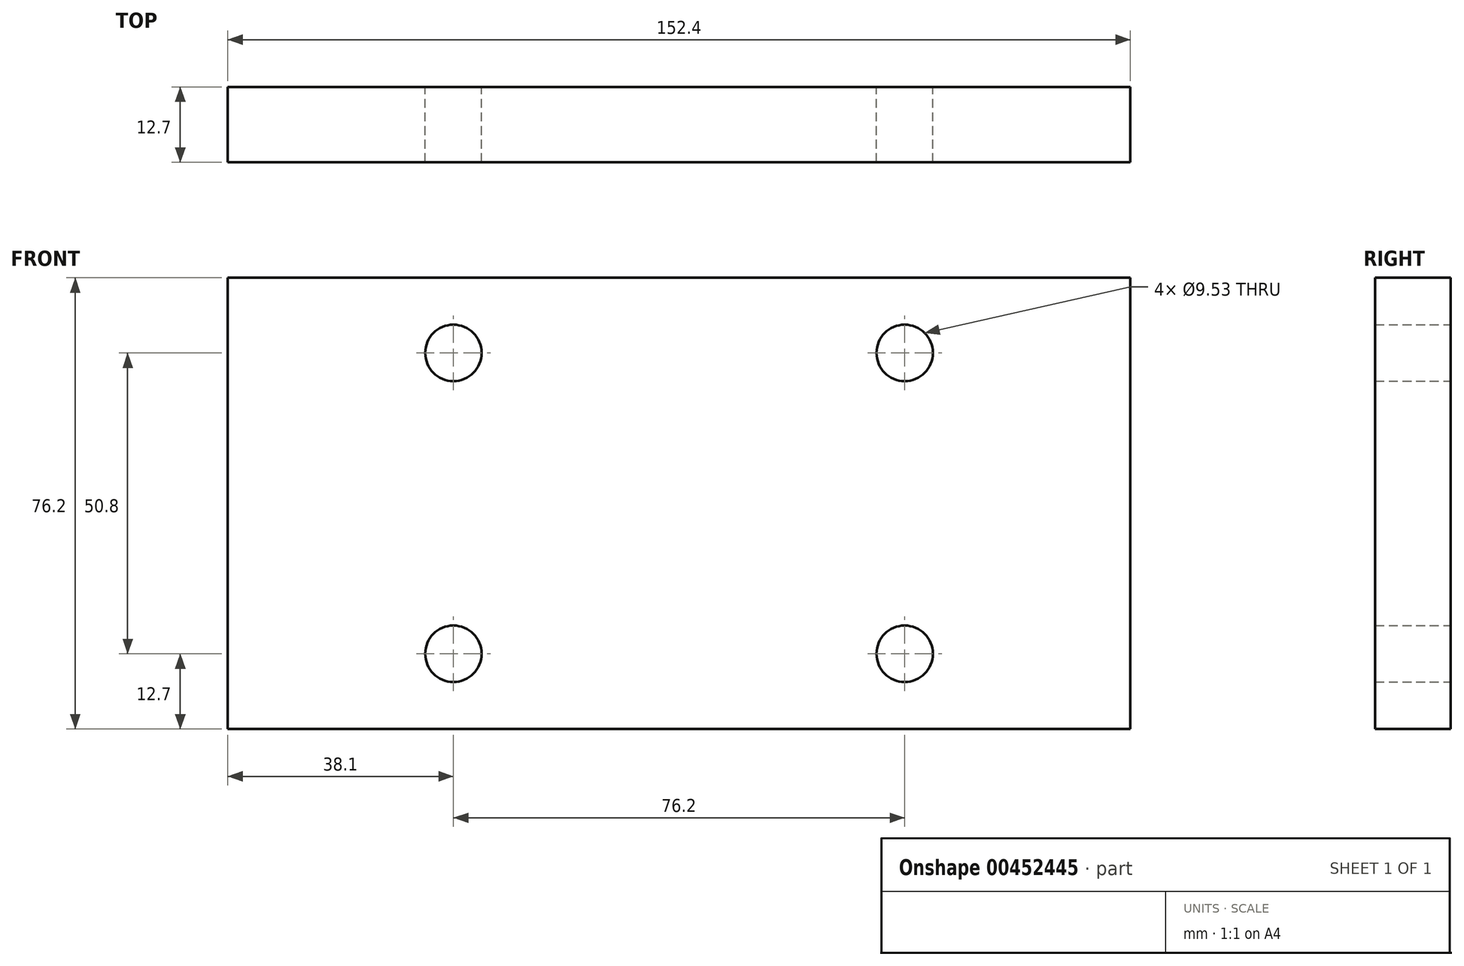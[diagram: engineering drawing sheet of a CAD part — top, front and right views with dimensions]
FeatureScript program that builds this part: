
annotation { "Feature Type Name" : "Feature", "Feature Type Description" : "" }
export const myFeature = defineFeature(function(context is Context, id is Id, definition is map)
    precondition{}
    {
        {
            var Q0;
            Q0=qCreatedBy(makeId("Front.planeOp"),FACE);
            var sketch = newSketch(context, id + "F0", { "sketchPlane" : qUnion([Q0])});
            skLineSegment(sketch, "E0.bottom", {"start": v(0, 0) * mm, "end": v(152.4, 0) * mm});
            skLineSegment(sketch, "E0.top", {"start": v(0, 76.2) * mm, "end": v(152.4, 76.2) * mm});
            skLineSegment(sketch, "E0.left", {"start": v(0, 0) * mm, "end": v(0, 76.2) * mm});
            skLineSegment(sketch, "E0.right", {"start": v(152.4, 0) * mm, "end": v(152.4, 76.2) * mm});
            skSolve(sketch);
        }
        {
            var Q0;
            Q0=makeQuery(id+"F0.imprint","IMPRINT",FACE,{"disambiguationData":[TD([[makeQuery(id+"F0.imprint","IMPRINT",EDGE,{"derivedFrom":sQuery(id+"F0.wireOp",EDGE,"E0.bottom")}),1.0]])]});
            extrude(context, id + "F1", {"entities" : qUnion([Q0]), "depth" : 12.7 * mm});
        }
        {
            var Q0;
            Q0=makeQuery(id+"F1.opExtrude","CAP_FACE",FACE,{"disambiguationData":[OSD([sQuery(id+"F0.wireOp",EDGE,"E0.bottom"),sQuery(id+"F0.wireOp",EDGE,"E0.top"),sQuery(id+"F0.wireOp",EDGE,"E0.left"),sQuery(id+"F0.wireOp",EDGE,"E0.right")])],"isStart":false});
            var sketch = newSketch(context, id + "F2", { "sketchPlane" : qUnion([Q0])});
            skLineSegment(sketch, "E1.bottom", {"start": v(38.1, 63.5) * mm, "end": v(114.3, 63.5) * mm, "construction": true});
            skLineSegment(sketch, "E1.top", {"start": v(38.1, 12.7) * mm, "end": v(114.3, 12.7) * mm, "construction": true});
            skLineSegment(sketch, "E1.left", {"start": v(38.1, 63.5) * mm, "end": v(38.1, 12.7) * mm, "construction": true});
            skLineSegment(sketch, "E1.right", {"start": v(114.3, 63.5) * mm, "end": v(114.3, 12.7) * mm, "construction": true});
            skLineSegment(sketch, "E2", {"start": v(152.4, 38.1) * mm, "end": v(0, 38.1) * mm, "construction": true});
            skLineSegment(sketch, "E3", {"start": v(76.2, 76.2) * mm, "end": v(76.2, 0) * mm, "construction": true});
            skSolve(sketch);
        }
        {
            var Q0;
            Q0=sQuery(id+"F2.wireOp",VERTEX,"E1.left.start");
            var Q1;
            Q1=sQuery(id+"F2.wireOp",VERTEX,"E1.left.end");
            var Q2;
            Q2=sQuery(id+"F2.wireOp",VERTEX,"E1.right.start");
            var Q3;
            Q3=sQuery(id+"F2.wireOp",VERTEX,"E1.top.end");
            var Q4;
            Q4=makeQuery(id+"F1.opExtrude","SWEPT_BODY",BODY,{"disambiguationData":[OSD([sQuery(id+"F0.wireOp",EDGE,"E0.bottom"),sQuery(id+"F0.wireOp",EDGE,"E0.top"),sQuery(id+"F0.wireOp",EDGE,"E0.left"),sQuery(id+"F0.wireOp",EDGE,"E0.right")])]});
            hole(context, id + "F3", {"style" : HoleStyle.SIMPLE, "endStyle" : HoleEndStyle.THROUGH, "holeDiameter" : 9.52 * mm, "isTappedThrough" : true, "tappedDepth" : 12.7 * mm, "tapClearance" : 3, "locations" : qUnion([Q0, Q1, Q2, Q3]), "scope" : qUnion([Q4])});
        }
    });
